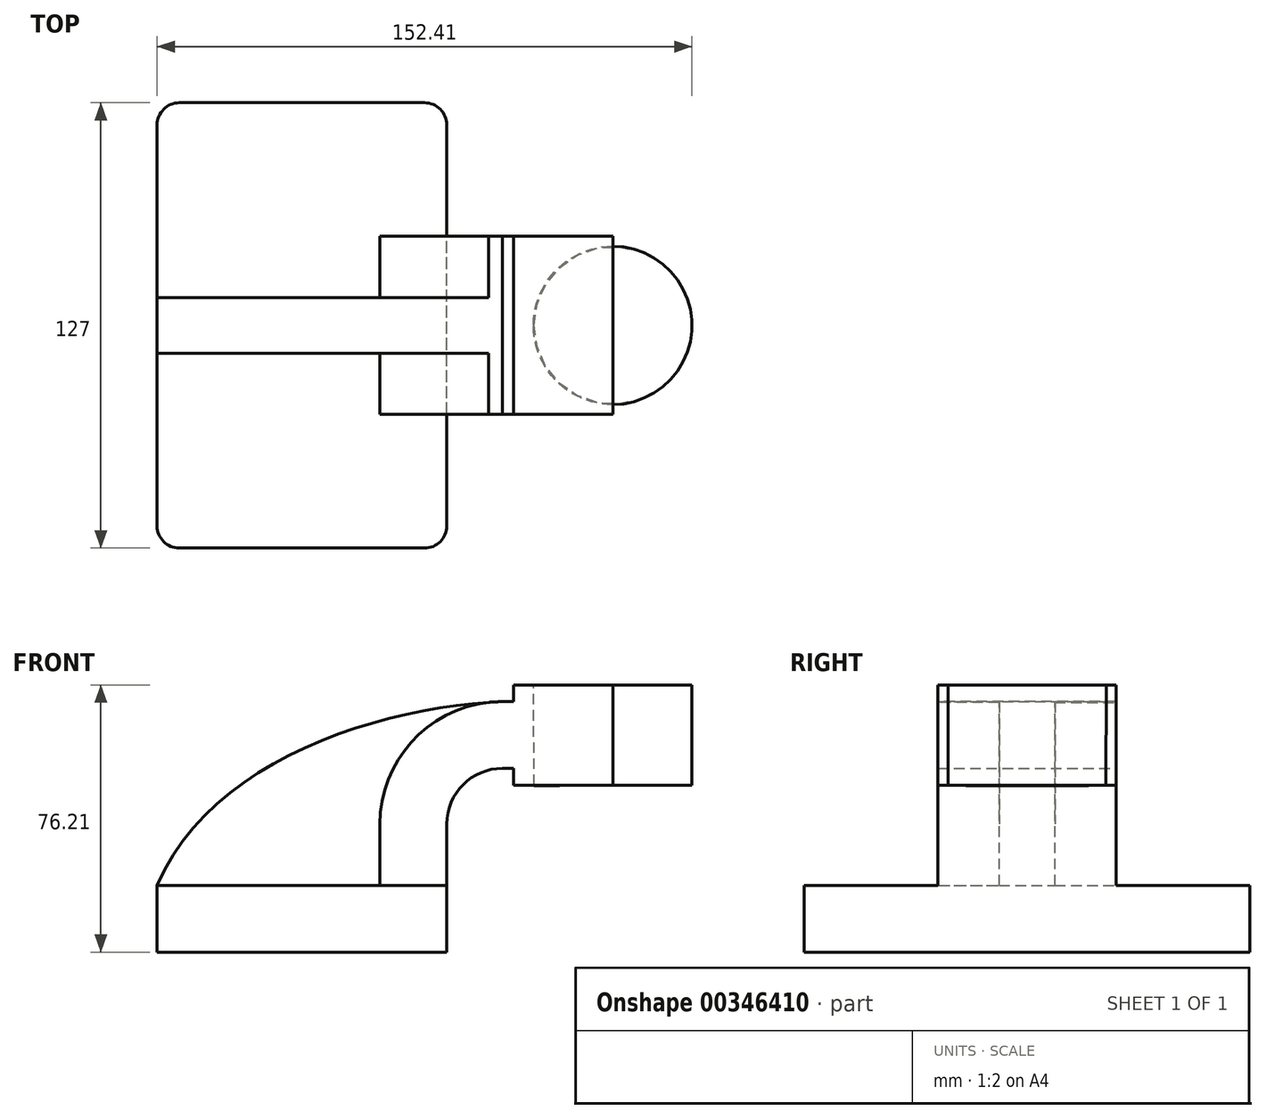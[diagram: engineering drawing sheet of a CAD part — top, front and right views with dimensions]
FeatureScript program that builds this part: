
annotation { "Feature Type Name" : "Feature", "Feature Type Description" : "" }
export const myFeature = defineFeature(function(context is Context, id is Id, definition is map)
    precondition{}
    {
        {
            var Q0;
            Q0=qCreatedBy(makeId("Front.planeOp"),FACE);
            var sketch = newSketch(context, id + "F0", { "sketchPlane" : qUnion([Q0])});
            skLineSegment(sketch, "E0.bottom", {"start": v(41.27, 9.53) * mm, "end": v(-41.28, 9.53) * mm});
            skLineSegment(sketch, "E0.top", {"start": v(41.28, -9.52) * mm, "end": v(-41.27, -9.52) * mm});
            skLineSegment(sketch, "E0.left", {"start": v(41.28, 9.53) * mm, "end": v(41.28, -9.52) * mm});
            skLineSegment(sketch, "E0.right", {"start": v(-41.28, 9.53) * mm, "end": v(-41.27, -9.52) * mm});
            skPoint(sketch, "E0.middle", {"position": v(0, 0) * mm});
            skLineSegment(sketch, "E1.bottom", {"start": v(111.12, 66.68) * mm, "end": v(60.32, 66.68) * mm});
            skLineSegment(sketch, "E1.top", {"start": v(111.12, 38.1) * mm, "end": v(60.32, 38.1) * mm});
            skLineSegment(sketch, "E1.left", {"start": v(111.12, 66.67) * mm, "end": v(111.12, 38.1) * mm});
            skLineSegment(sketch, "E1.right", {"start": v(60.32, 66.67) * mm, "end": v(60.32, 38.1) * mm});
            skPoint(sketch, "E1.middle", {"position": v(85.72, 52.39) * mm});
            skLineSegment(sketch, "E2", {"start": v(41.27, 9.53) * mm, "end": v(41.27, 27) * mm});
            skArc(sketch, "E3", {"start": v(41.27, 27) * mm, "mid": v(45.92, 38.23) * mm, "end": v(57.15, 42.88) * mm});
            skLineSegment(sketch, "E4", {"start": v(57.15, 42.88) * mm, "end": v(88.55, 42.88) * mm});
            skLineSegment(sketch, "E5.0", {"start": v(57.15, 61.93) * mm, "end": v(88.55, 61.93) * mm});
            skArc(sketch, "E5.1", {"start": v(22.23, 27) * mm, "mid": v(32.45, 51.7) * mm, "end": v(57.15, 61.93) * mm});
            skLineSegment(sketch, "E5.2", {"start": v(22.22, 9.53) * mm, "end": v(22.22, 27) * mm});
            skLineSegment(sketch, "E6", {"start": v(88.64, 38.1) * mm, "end": v(88.55, 66.68) * mm});
            skFitSpline(sketch, "E7", {"points": [v(-41.28, 9.53) * mm, v(57.15, 61.93) * mm], "startDerivative": vector(45.8, 107.68) * mm, "endDerivative": vector(104.42, 4.46) * mm});
            skSolve(sketch);
        }
        {
            var Q0;
            Q0=makeQuery(id+"F0.imprint","IMPRINT",FACE,{"disambiguationData":[TD([[makeQuery(id+"F0.imprint","IMPRINT",EDGE,{"derivedFrom":sQuery(id+"F0.wireOp",EDGE,"E0.top")}),-1.0]])]});
            extrude(context, id + "F1", {"entities" : qUnion([Q0]), "endBound" : BoundingType.SYMMETRIC, "depth" : 127 * mm});
        }
        {
            var Q0;
            {var subQ1=sQuery(id+"F0.wireOp",EDGE,"E2");Q0=makeQuery(id+"F0.imprint","IMPRINT",FACE,{"disambiguationData":[TD([[makeQuery(id+"F0.imprint","IMPRINT",EDGE,{"derivedFrom":subQ1}),1.0]])]});}
            var Q1;
            {var subQ6=sQuery(id+"F0.wireOp",EDGE,"E6");Q1=makeQuery(id+"F0.imprint","IMPRINT",FACE,{"disambiguationData":[TD([[makeQuery(id+"F0.imprint","IMPRINT",EDGE,{"derivedFrom":subQ6}),1.0]])]});}
            extrude(context, id + "F2", {"entities" : qUnion([Q0, Q1]), "operationType" : NewBodyOperationType.ADD, "endBound" : BoundingType.SYMMETRIC, "depth" : 50.8 * mm});
        }
        {
            var Q0;
            {var subQ3=sQuery(id+"F0.wireOp",EDGE,"E5.2");Q0=makeQuery(id+"F0.imprint","IMPRINT",FACE,{"disambiguationData":[TD([[makeQuery(id+"F0.imprint","IMPRINT",EDGE,{"derivedFrom":subQ3}),1.0]])]});}
            extrude(context, id + "F3", {"entities" : qUnion([Q0]), "operationType" : NewBodyOperationType.ADD, "endBound" : BoundingType.SYMMETRIC, "depth" : 15.88 * mm});
        }
        {
            var Q0;
            {var subQ0=sQuery(id+"F0.wireOp",EDGE,"E1.left");Q0=makeQuery(id+"F0.imprint","IMPRINT",FACE,{"disambiguationData":[TD([[makeQuery(id+"F0.imprint","IMPRINT",EDGE,{"derivedFrom":subQ0}),-1.0]])]});}
            var Q1;
            Q1=sQuery(id+"F0.wireOp",EDGE,"E6");
            revolve(context, id + "F4", {"entities" : qUnion([Q0]), "axis" : qUnion([Q1]), "revolveType" : RevolveType.FULL});
        }
        {
            var Q0;
            Q0=makeQuery(id+"F1.opExtrude","CAP_EDGE",EDGE,{"disambiguationData":[OSD([sQuery(id+"F0.wireOp",EDGE,"E0.left")])],"isStart":false});
            var Q1;
            Q1=makeQuery(id+"F1.opExtrude","CAP_EDGE",EDGE,{"disambiguationData":[OSD([sQuery(id+"F0.wireOp",EDGE,"E0.right")])],"isStart":false});
            var Q2;
            Q2=makeQuery(id+"F1.opExtrude","CAP_EDGE",EDGE,{"disambiguationData":[OSD([sQuery(id+"F0.wireOp",EDGE,"E0.left")])],"isStart":true});
            var Q3;
            Q3=makeQuery(id+"F1.opExtrude","CAP_EDGE",EDGE,{"disambiguationData":[OSD([sQuery(id+"F0.wireOp",EDGE,"E0.right")])],"isStart":true});
            fillet(context, id + "F5", {"entities" : qUnion([Q0, Q1, Q2, Q3]), "radius" : 6.35 * mm, "tangentPropagation" : true, "allowEdgeOverflow" : false});
        }
    });
